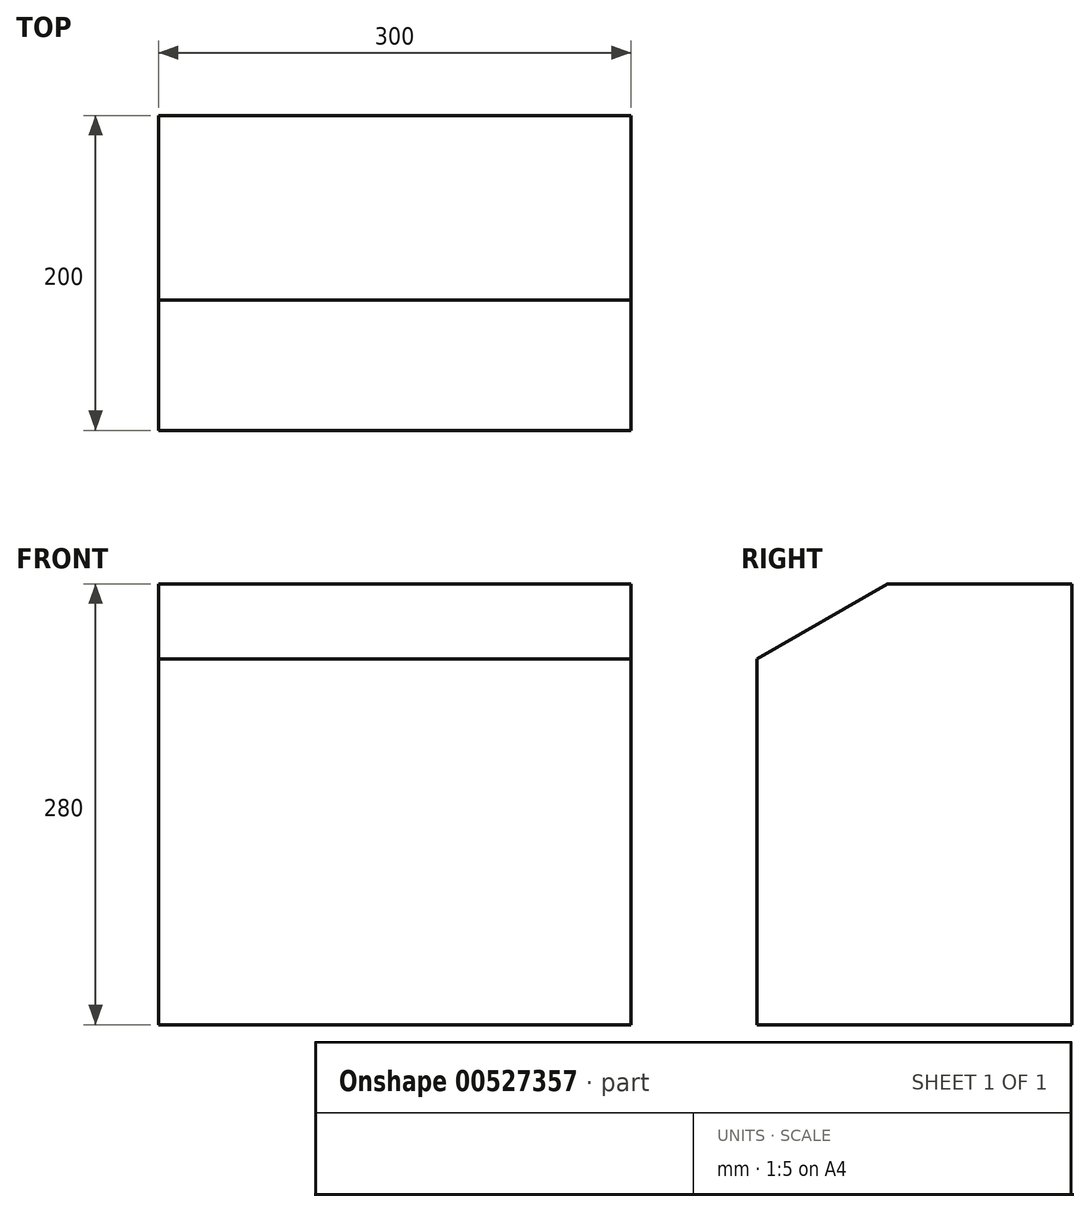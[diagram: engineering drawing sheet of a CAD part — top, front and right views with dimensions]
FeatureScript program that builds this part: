
annotation { "Feature Type Name" : "Feature", "Feature Type Description" : "" }
export const myFeature = defineFeature(function(context is Context, id is Id, definition is map)
    precondition{}
    {
        {
            var Q0;
            Q0=qCreatedBy(makeId("Top.planeOp"),FACE);
            var sketch = newSketch(context, id + "F0", { "sketchPlane" : qUnion([Q0])});
            skLineSegment(sketch, "E0.bottom", {"start": v(-150, 100) * mm, "end": v(150, 100) * mm});
            skLineSegment(sketch, "E0.top", {"start": v(-150, -100) * mm, "end": v(150, -100) * mm});
            skLineSegment(sketch, "E0.left", {"start": v(-150, 100) * mm, "end": v(-150, -100) * mm});
            skLineSegment(sketch, "E0.right", {"start": v(150, 100) * mm, "end": v(150, -100) * mm});
            skPoint(sketch, "E1", {"position": v(150, 0) * mm});
            skPoint(sketch, "E2", {"position": v(0, 100) * mm});
            skSolve(sketch);
        }
        {
            var Q0;
            Q0=qCreatedBy(makeId("Right.planeOp"),FACE);
            var sketch = newSketch(context, id + "F1", { "sketchPlane" : qUnion([Q0])});
            skLineSegment(sketch, "E3", {"start": v(-100, 0) * mm, "end": v(-100, 232.14) * mm});
            skLineSegment(sketch, "E4", {"start": v(-100, 232.14) * mm, "end": v(-17.11, 280) * mm});
            skLineSegment(sketch, "E5", {"start": v(-17.11, 280) * mm, "end": v(100, 280) * mm});
            skLineSegment(sketch, "E6", {"start": v(100, 280) * mm, "end": v(100, 0) * mm});
            skLineSegment(sketch, "E7", {"start": v(-100, 0) * mm, "end": v(100, 0) * mm});
            skSolve(sketch);
        }
        {
            var Q0;
            Q0=sQuery(id+"F0.wireOp",EDGE,"E0.top");
            var Q1;
            Q1=qCreatedBy(makeId("Front.planeOp"),FACE);
            cPlane(context, id + "F2", {"entities" : qUnion([Q0, Q1]), "cplaneType" : CPlaneType.LINE_ANGLE, "offset" : 25 * mm, "angle" : 0 * degree, "width" : 150 * mm, "height" : 150 * mm});
        }
        {
            var Q0;
            Q0=makeQuery(id+"F1.imprint","IMPRINT",FACE,{"disambiguationData":[TD([[makeQuery(id+"F1.imprint","IMPRINT",EDGE,{"derivedFrom":sQuery(id+"F1.wireOp",EDGE,"E3")}),-1.0]])]});
            var Q1;
            Q1=sQuery(id+"F1.wireOp",EDGE,"E5");
            var Q2;
            Q2=sQuery(id+"F1.wireOp",EDGE,"E4");
            var Q3;
            Q3=sQuery(id+"F1.wireOp",EDGE,"E3");
            var Q4;
            Q4=sQuery(id+"F1.wireOp",EDGE,"E6");
            var Q5;
            Q5=sQuery(id+"F1.wireOp",EDGE,"E7");
            var Q6;
            Q6=sQuery(id+"F0.wireOp",VERTEX,"E0.right.start");
            var Q7;
            Q7=sQuery(id+"F0.wireOp",VERTEX,"E0.bottom.start");
            extrude(context, id + "F3", {"entities" : qUnion([Q0]), "bodyType" : ToolBodyType.SURFACE, "surfaceEntities" : qUnion([Q1, Q2, Q3, Q4, Q5]), "endBound" : BoundingType.UP_TO_VERTEX, "depth" : 25 * mm, "endBoundEntityVertex" : qUnion([Q6]), "offsetDistance" : 25 * mm, "hasSecondDirection" : true, "secondDirectionBound" : SecondDirectionBoundingType.UP_TO_VERTEX, "secondDirectionOppositeDirection" : true, "secondDirectionDepth" : 25 * mm, "secondDirectionBoundEntityVertex" : qUnion([Q7])});
        }
    });
